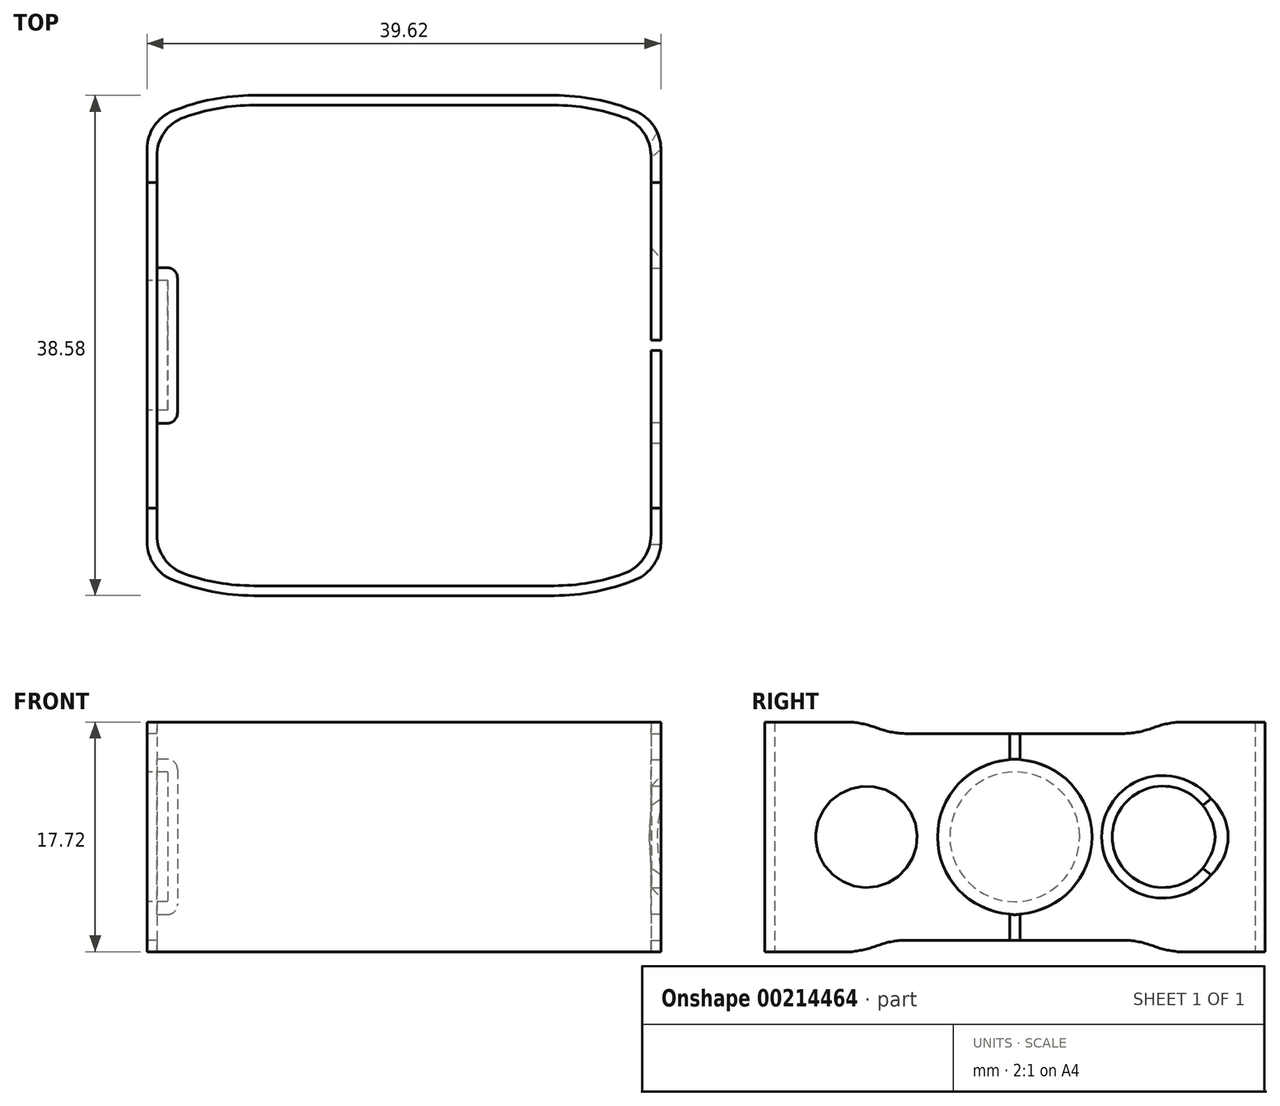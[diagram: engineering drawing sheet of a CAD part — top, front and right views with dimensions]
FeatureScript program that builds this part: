
annotation { "Feature Type Name" : "Feature", "Feature Type Description" : "" }
export const myFeature = defineFeature(function(context is Context, id is Id, definition is map)
    precondition{}
    {
        {
            var Q0;
            Q0=qCreatedBy(makeId("Top.planeOp"),FACE);
            var sketch = newSketch(context, id + "F0", { "sketchPlane" : qUnion([Q0])});
            skLineSegment(sketch, "E0.bottom", {"start": v(19.05, 16.67) * mm, "end": v(-19.05, 16.67) * mm});
            skLineSegment(sketch, "E0.top", {"start": v(19.05, -16.67) * mm, "end": v(-19.05, -16.67) * mm});
            skLineSegment(sketch, "E0.left", {"start": v(19.05, 14.61) * mm, "end": v(19.05, -14.61) * mm});
            skLineSegment(sketch, "E0.right", {"start": v(-19.05, 14.61) * mm, "end": v(-19.05, -14.61) * mm});
            skPoint(sketch, "E0.middle", {"position": v(0, 0) * mm});
            skLineSegment(sketch, "E1", {"start": v(-29.61, 0) * mm, "end": v(26.31, 0) * mm, "construction": true});
            skPoint(sketch, "E1.startSnap0", {"position": v(-19.05, 0) * mm});
            skLineSegment(sketch, "E2", {"start": v(-11.59, 18.53) * mm, "end": v(0, 18.53) * mm});
            skLineSegment(sketch, "E3", {"start": v(0, 18.53) * mm, "end": v(11.59, 18.53) * mm});
            skArc(sketch, "E4", {"start": v(-11.59, 18.53) * mm, "mid": v(-14.3, 18.3) * mm, "end": v(-16.95, 17.6) * mm});
            skArc(sketch, "E5", {"start": v(16.95, 17.6) * mm, "mid": v(14.3, 18.3) * mm, "end": v(11.59, 18.53) * mm});
            skArc(sketch, "E6.MirrorCS", {"start": v(-11.59, -18.53) * mm, "mid": v(-14.3, -18.3) * mm, "end": v(-16.95, -17.6) * mm});
            skLineSegment(sketch, "E7.MirrorCS", {"start": v(-11.59, -18.53) * mm, "end": v(0, -18.53) * mm});
            skLineSegment(sketch, "E8.MirrorCS", {"start": v(0, -18.53) * mm, "end": v(11.59, -18.53) * mm});
            skArc(sketch, "E9.MirrorCS", {"start": v(16.95, -17.6) * mm, "mid": v(14.3, -18.3) * mm, "end": v(11.59, -18.53) * mm});
            skLineSegment(sketch, "E10.0", {"start": v(-11.59, 19.3) * mm, "end": v(0, 19.3) * mm});
            skLineSegment(sketch, "E10.1", {"start": v(0, 19.3) * mm, "end": v(11.59, 19.3) * mm});
            skArc(sketch, "E10.2", {"start": v(-11.59, 19.3) * mm, "mid": v(-14.77, 18.99) * mm, "end": v(-17.83, 18.08) * mm});
            skArc(sketch, "E10.3", {"start": v(17.83, 18.08) * mm, "mid": v(14.77, 18.99) * mm, "end": v(11.59, 19.3) * mm});
            skLineSegment(sketch, "E10.4", {"start": v(19.81, 15.14) * mm, "end": v(19.81, -15.14) * mm});
            skArc(sketch, "E10.5", {"start": v(17.83, -18.08) * mm, "mid": v(14.77, -18.99) * mm, "end": v(11.59, -19.3) * mm});
            skLineSegment(sketch, "E10.6", {"start": v(-19.81, 15.14) * mm, "end": v(-19.81, -15.14) * mm});
            skArc(sketch, "E10.7", {"start": v(-11.59, -19.3) * mm, "mid": v(-14.77, -18.99) * mm, "end": v(-17.83, -18.08) * mm});
            skLineSegment(sketch, "E10.8", {"start": v(-11.59, -19.3) * mm, "end": v(0, -19.3) * mm});
            skLineSegment(sketch, "E10.9", {"start": v(0, -19.3) * mm, "end": v(11.59, -19.3) * mm});
            skPoint(sketch, "E11.visualSharp", {"position": v(-19.05, 16.67) * mm});
            skArc(sketch, "E11.filletArc", {"start": v(-16.95, 17.6) * mm, "mid": v(-18.47, 16.44) * mm, "end": v(-19.05, 14.61) * mm});
            skPoint(sketch, "E12.visualSharp", {"position": v(-19.81, 17.12) * mm});
            skArc(sketch, "E12.filletArc", {"start": v(-17.83, 18.08) * mm, "mid": v(-19.27, 16.91) * mm, "end": v(-19.81, 15.14) * mm});
            skPoint(sketch, "E13.visualSharp", {"position": v(19.05, 16.67) * mm});
            skArc(sketch, "E13.filletArc", {"start": v(19.05, 14.61) * mm, "mid": v(18.47, 16.44) * mm, "end": v(16.95, 17.6) * mm});
            skPoint(sketch, "E14.visualSharp", {"position": v(19.81, 17.12) * mm});
            skArc(sketch, "E14.filletArc", {"start": v(19.81, 15.14) * mm, "mid": v(19.27, 16.91) * mm, "end": v(17.83, 18.08) * mm});
            skPoint(sketch, "E15.visualSharp", {"position": v(19.05, -16.67) * mm});
            skArc(sketch, "E15.filletArc", {"start": v(16.95, -17.6) * mm, "mid": v(18.47, -16.44) * mm, "end": v(19.05, -14.61) * mm});
            skPoint(sketch, "E16.visualSharp", {"position": v(19.81, -17.12) * mm});
            skArc(sketch, "E16.filletArc", {"start": v(17.83, -18.08) * mm, "mid": v(19.27, -16.91) * mm, "end": v(19.81, -15.14) * mm});
            skPoint(sketch, "E17.visualSharp", {"position": v(-19.05, -16.67) * mm});
            skArc(sketch, "E17.filletArc", {"start": v(-19.05, -14.61) * mm, "mid": v(-18.47, -16.44) * mm, "end": v(-16.95, -17.6) * mm});
            skPoint(sketch, "E18.visualSharp", {"position": v(-19.81, -17.12) * mm});
            skArc(sketch, "E18.filletArc", {"start": v(-19.81, -15.14) * mm, "mid": v(-19.27, -16.91) * mm, "end": v(-17.83, -18.08) * mm});
            skSolve(sketch);
        }
        {
            var Q0;
            Q0=makeQuery(id+"F0.imprint","IMPRINT",FACE,{"disambiguationData":[TD([[makeQuery(id+"F0.imprint","IMPRINT",EDGE,{"derivedFrom":sQuery(id+"F0.wireOp",EDGE,"E0.left")}),1.0]])]});
            extrude(context, id + "F1", {"entities" : qUnion([Q0]), "endBound" : BoundingType.SYMMETRIC, "depth" : 17.72 * mm});
        }
        {
            var Q0;
            Q0=makeQuery(id+"F1.opExtrude","SWEPT_FACE",FACE,{"disambiguationData":[OSD([sQuery(id+"F0.wireOp",EDGE,"E10.4")])]});
            var sketch = newSketch(context, id + "F2", { "sketchPlane" : qUnion([Q0])});
            skCircle(sketch, "E19", {"center": v(0, 0) * mm, "radius": 5.95 * mm});
            skLineSegment(sketch, "E20.bottom", {"start": v(0.4, 16.24) * mm, "end": v(-0.4, 16.24) * mm});
            skLineSegment(sketch, "E20.top", {"start": v(0.4, -16.24) * mm, "end": v(-0.4, -16.24) * mm});
            skLineSegment(sketch, "E20.left", {"start": v(0.4, 16.24) * mm, "end": v(0.4, -16.24) * mm});
            skLineSegment(sketch, "E20.right", {"start": v(-0.4, 16.24) * mm, "end": v(-0.4, -16.24) * mm});
            skCircle(sketch, "E21", {"center": v(-11.43, 0) * mm, "radius": 3.9 * mm});
            skLineSegment(sketch, "E22", {"start": v(0, 20.34) * mm, "end": v(0, -24.58) * mm, "construction": true});
            skPoint(sketch, "E22.startSnap0", {"position": v(0, 8.86) * mm});
            skCircle(sketch, "E23.MirrorC", {"center": v(11.43, 0) * mm, "radius": 3.9 * mm});
            skSolve(sketch);
        }
        {
            var Q0;
            Q0=qSketchRegion(id+"F2",true);
            extrude(context, id + "F3", {"entities" : qUnion([Q0]), "operationType" : NewBodyOperationType.REMOVE, "oppositeDirection" : true, "depth" : 25.4 * mm});
        }
        {
            var Q0;
            Q0=qSketchRegion(id+"F2",true);
            extrude(context, id + "F4", {"entities" : qUnion([Q0]), "operationType" : NewBodyOperationType.REMOVE, "oppositeDirection" : true, "depth" : 25.4 * mm});
        }
        {
            var Q0;
            Q0=makeQuery(id+"F3.boolean.opBoolean","COPY",EDGE,{"derivedFrom":makeQuery(id+"F3.opExtrude","CAP_EDGE",EDGE,{"disambiguationData":[OSD([sQuery(id+"F2.wireOp",EDGE,"E21")])],"isStart":true})});
            var Q1;
            Q1=makeQuery(id+"F3.boolean.opBoolean","COPY",EDGE,{"derivedFrom":makeQuery(id+"F3.opExtrude","CAP_EDGE",EDGE,{"disambiguationData":[OSD([sQuery(id+"F2.wireOp",EDGE,"E23.MirrorC")])],"isStart":true})});
            chamfer(context, id + "F5", {"entities" : qUnion([Q0, Q1]), "chamferType" : ChamferType.OFFSET_ANGLE, "width" : 0.71 * mm, "oppositeDirection" : false, "angle" : 49 * degree, "tangentPropagation" : true});
        }
        {
            var Q0;
            Q0=makeQuery(id+"F1.opExtrude","SWEPT_FACE",FACE,{"disambiguationData":[OSD([sQuery(id+"F0.wireOp",EDGE,"E10.6")])]});
            var sketch = newSketch(context, id + "F6", { "sketchPlane" : qUnion([Q0])});
            skCircle(sketch, "E24", {"center": v(0, 0) * mm, "radius": 6 * mm});
            skSolve(sketch);
        }
        {
            var Q0;
            Q0=qSketchRegion(id+"F6",true);
            extrude(context, id + "F7", {"entities" : qUnion([Q0]), "operationType" : NewBodyOperationType.ADD, "oppositeDirection" : true, "depth" : 2.35 * mm});
        }
        {
            var Q0;
            Q0=makeQuery(id+"F1.opExtrude","SWEPT_FACE",FACE,{"disambiguationData":[OSD([sQuery(id+"F0.wireOp",EDGE,"E10.6")])]});
            var sketch = newSketch(context, id + "F8", { "sketchPlane" : qUnion([Q0])});
            skCircle(sketch, "E25", {"center": v(0, 0) * mm, "radius": 5 * mm});
            skSolve(sketch);
        }
        {
            var Q0;
            Q0=qSketchRegion(id+"F8",true);
            extrude(context, id + "F9", {"entities" : qUnion([Q0]), "operationType" : NewBodyOperationType.REMOVE, "oppositeDirection" : true, "depth" : 1.59 * mm});
        }
        {
            var Q0;
            Q0=makeQuery(id+"F9.boolean.opBoolean","COPY",EDGE,{"derivedFrom":makeQuery(id+"F9.opExtrude","CAP_EDGE",EDGE,{"disambiguationData":[OSD([sQuery(id+"F8.wireOp",EDGE,"E25")])],"isStart":true})});
            var Q1;
            Q1=makeQuery(id+"F7.opExtrude","CAP_EDGE",EDGE,{"disambiguationData":[OSD([sQuery(id+"F6.wireOp",EDGE,"E24")])],"isStart":false});
            fillet(context, id + "F10", {"entities" : qUnion([Q0, Q1]), "radius" : 0.8 * mm, "tangentPropagation" : true, "allowEdgeOverflow" : false});
        }
        {
            var Q0;
            Q0=makeQuery(id+"F1.opExtrude","SWEPT_FACE",FACE,{"disambiguationData":[OSD([sQuery(id+"F0.wireOp",EDGE,"E10.6")])]});
            var sketch = newSketch(context, id + "F11", { "sketchPlane" : qUnion([Q0])});
            skLineSegment(sketch, "E26", {"start": v(-8.32, 7.97) * mm, "end": v(8.32, 7.97) * mm});
            skLineSegment(sketch, "E27", {"start": v(0, 3.4) * mm, "end": v(0, -3) * mm, "construction": true});
            skLineSegment(sketch, "E28", {"start": v(-2.44, 0) * mm, "end": v(2.9, 0) * mm, "construction": true});
            skArc(sketch, "E29", {"start": v(-10.53, 8.37) * mm, "mid": v(-9.44, 8.07) * mm, "end": v(-8.32, 7.97) * mm});
            skArc(sketch, "E30", {"start": v(-10.53, 8.37) * mm, "mid": v(-12.05, 8.78) * mm, "end": v(-13.62, 8.92) * mm});
            skArc(sketch, "E31.MirrorCS", {"start": v(10.53, 8.37) * mm, "mid": v(12.05, 8.78) * mm, "end": v(13.62, 8.92) * mm});
            skArc(sketch, "E32.MirrorCS", {"start": v(10.53, 8.37) * mm, "mid": v(9.44, 8.07) * mm, "end": v(8.32, 7.97) * mm});
            skLineSegment(sketch, "E33", {"start": v(-13.62, 8.92) * mm, "end": v(13.62, 8.92) * mm});
            skLineSegment(sketch, "E34", {"start": v(-13.62, 8.92) * mm, "end": v(-24.45, 8.92) * mm, "construction": true});
            skLineSegment(sketch, "E35.MirrorCS", {"start": v(-8.32, -7.97) * mm, "end": v(8.32, -7.97) * mm});
            skLineSegment(sketch, "E36.MirrorCS", {"start": v(-13.62, -8.92) * mm, "end": v(-24.45, -8.92) * mm, "construction": true});
            skArc(sketch, "E37.MirrorCS", {"start": v(-10.53, -8.37) * mm, "mid": v(-9.44, -8.07) * mm, "end": v(-8.32, -7.97) * mm});
            skLineSegment(sketch, "E38.MirrorCS", {"start": v(-13.62, -8.92) * mm, "end": v(13.62, -8.92) * mm});
            skArc(sketch, "E39.MirrorCS", {"start": v(10.53, -8.37) * mm, "mid": v(12.05, -8.78) * mm, "end": v(13.62, -8.92) * mm});
            skArc(sketch, "E40.MirrorCS", {"start": v(10.53, -8.37) * mm, "mid": v(9.44, -8.07) * mm, "end": v(8.32, -7.97) * mm});
            skArc(sketch, "E41.MirrorCS", {"start": v(-10.53, -8.37) * mm, "mid": v(-12.05, -8.78) * mm, "end": v(-13.62, -8.92) * mm});
            skSolve(sketch);
        }
        {
            var Q0;
            Q0=qSketchRegion(id+"F11",true);
            extrude(context, id + "F12", {"entities" : qUnion([Q0]), "operationType" : NewBodyOperationType.REMOVE, "endBound" : BoundingType.THROUGH_ALL, "oppositeDirection" : true, "depth" : 25.4 * mm});
        }
    });
